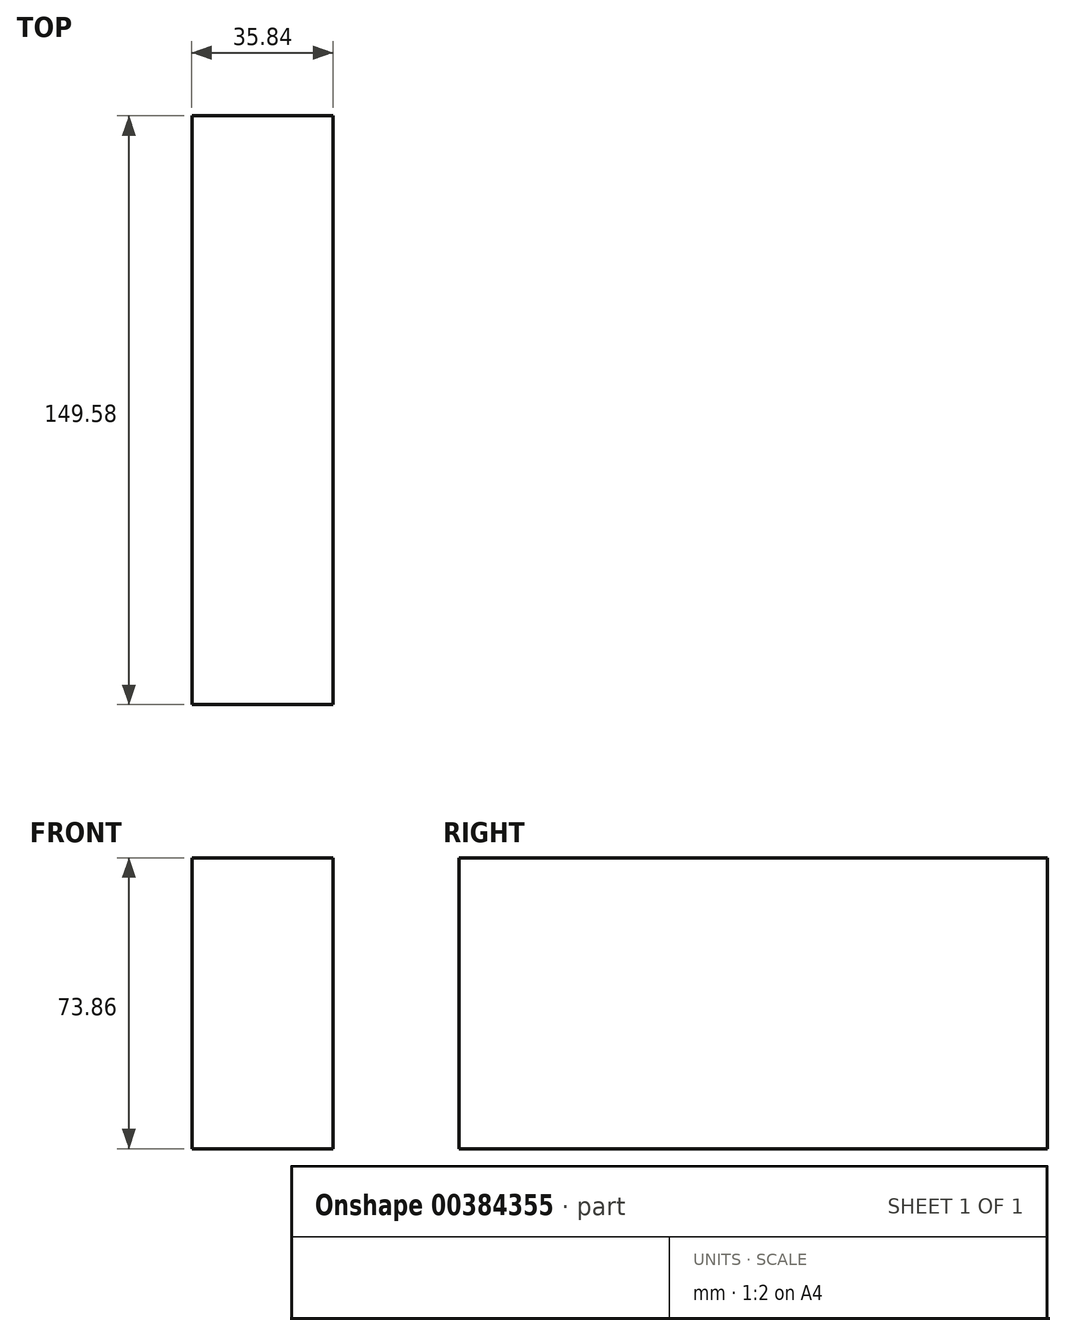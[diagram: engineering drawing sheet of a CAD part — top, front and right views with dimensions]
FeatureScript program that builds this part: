
annotation { "Feature Type Name" : "Feature", "Feature Type Description" : "" }
export const myFeature = defineFeature(function(context is Context, id is Id, definition is map)
    precondition{}
    {
        {
            var Q0;
            Q0=qCreatedBy(makeId("Front.planeOp"),FACE);
            var sketch = newSketch(context, id + "F0", { "sketchPlane" : qUnion([Q0])});
            skLineSegment(sketch, "E0.bottom", {"start": v(0, 0) * mm, "end": v(0, 0) * mm});
            skLineSegment(sketch, "E0.top", {"start": v(0, 0) * mm, "end": v(0, 0) * mm});
            skLineSegment(sketch, "E0.left", {"start": v(0, 0) * mm, "end": v(0, 0) * mm});
            skLineSegment(sketch, "E0.right", {"start": v(0, 0) * mm, "end": v(0, 0) * mm});
            skLineSegment(sketch, "E1.bottom", {"start": v(84.38, 73.86) * mm, "end": v(48.54, 73.86) * mm});
            skLineSegment(sketch, "E1.top", {"start": v(84.38, 0) * mm, "end": v(48.54, 0) * mm});
            skLineSegment(sketch, "E1.left", {"start": v(84.38, 73.86) * mm, "end": v(84.38, 0) * mm});
            skLineSegment(sketch, "E1.right", {"start": v(48.54, 73.86) * mm, "end": v(48.54, 0) * mm});
            skSolve(sketch);
        }
        {
            var Q0;
            Q0=makeQuery(id+"F0.imprint","IMPRINT",FACE,{"disambiguationData":[TD([[makeQuery(id+"F0.imprint","IMPRINT",EDGE,{"derivedFrom":sQuery(id+"F0.wireOp",EDGE,"E1.bottom")}),1.0]])]});
            extrude(context, id + "F1", {"entities" : qUnion([Q0]), "depth" : 149.58 * mm});
        }
    });
